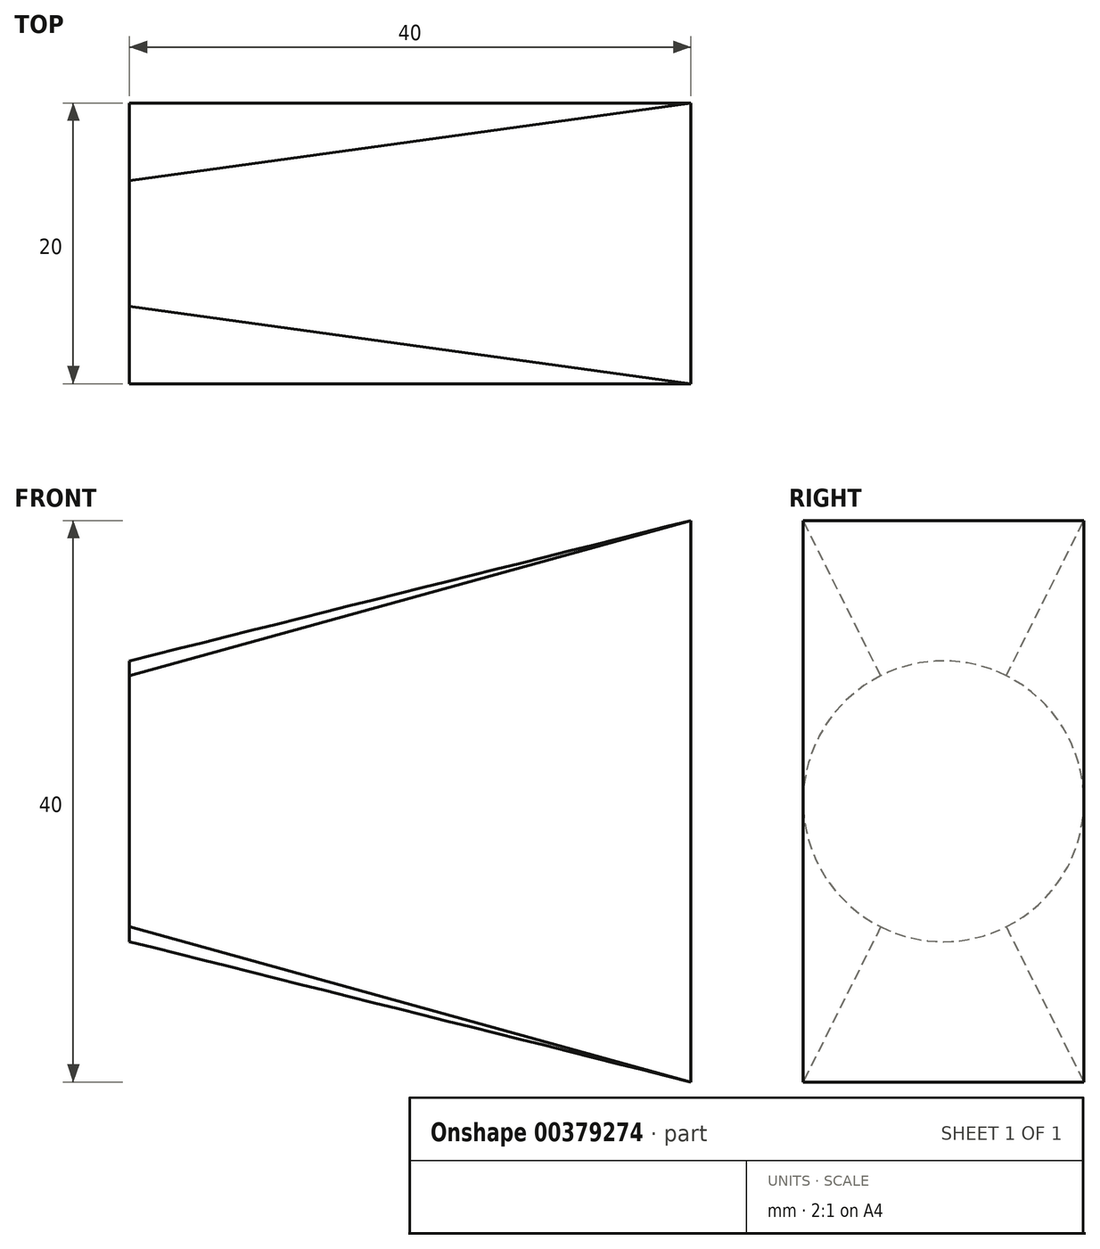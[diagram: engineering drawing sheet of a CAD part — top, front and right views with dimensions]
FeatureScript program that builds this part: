
annotation { "Feature Type Name" : "Feature", "Feature Type Description" : "" }
export const myFeature = defineFeature(function(context is Context, id is Id, definition is map)
    precondition{}
    {
        {
            var Q0;
            Q0=qCreatedBy(makeId("Right.planeOp"),FACE);
            var sketch = newSketch(context, id + "F0", { "sketchPlane" : qUnion([Q0])});
            skPoint(sketch, "E0.middle", {"position": v(0, 0) * mm});
            skArc(sketch, "E1", {"start": v(4.47, 8.94) * mm, "mid": v(0, 10) * mm, "end": v(-4.47, 8.94) * mm});
            skArc(sketch, "E2", {"start": v(-4.47, 8.94) * mm, "mid": v(-10, 0) * mm, "end": v(-4.47, -8.94) * mm});
            skArc(sketch, "E3", {"start": v(-4.47, -8.94) * mm, "mid": v(0, -10) * mm, "end": v(4.47, -8.94) * mm});
            skArc(sketch, "E4", {"start": v(4.47, -8.94) * mm, "mid": v(10, 0) * mm, "end": v(4.47, 8.94) * mm});
            skSolve(sketch);
        }
        {
            var Q0;
            Q0=qCreatedBy(makeId("Right.planeOp"),FACE);
            cPlane(context, id + "F1", {"entities" : qUnion([Q0]), "cplaneType" : CPlaneType.OFFSET, "offset" : 40 * mm, "width" : 150 * mm, "height" : 150 * mm});
        }
        {
            var Q0;
            Q0=qCreatedBy(id+"F1.planeOp",FACE);
            var sketch = newSketch(context, id + "F2", { "sketchPlane" : qUnion([Q0])});
            skLineSegment(sketch, "E5.bottom", {"start": v(-10, 20) * mm, "end": v(10, 20) * mm});
            skLineSegment(sketch, "E5.top", {"start": v(-10, -20) * mm, "end": v(10, -20) * mm});
            skLineSegment(sketch, "E5.left", {"start": v(-10, 20) * mm, "end": v(-10, -20) * mm});
            skLineSegment(sketch, "E5.right", {"start": v(10, 20) * mm, "end": v(10, -20) * mm});
            skPoint(sketch, "E5.middle", {"position": v(0, 0) * mm});
            skSolve(sketch);
        }
        {
            var Q0;
            Q0=makeQuery(id+"F0.imprint","IMPRINT",FACE,{"disambiguationData":[TD([[makeQuery(id+"F0.imprint","IMPRINT",EDGE,{"derivedFrom":sQuery(id+"F0.wireOp",EDGE,"E1")}),1.0]])]});
            var Q1;
            Q1=makeQuery(id+"F2.imprint","IMPRINT",FACE,{"disambiguationData":[TD([[makeQuery(id+"F2.imprint","IMPRINT",EDGE,{"derivedFrom":sQuery(id+"F2.wireOp",EDGE,"E5.bottom")}),-1.0]])]});
            loft(context, id + "F3", {"sheetProfilesArray" : [{ "sheetProfileEntities" : qUnion([Q0]) }, { "sheetProfileEntities" : qUnion([Q1]) }]});
        }
    });
